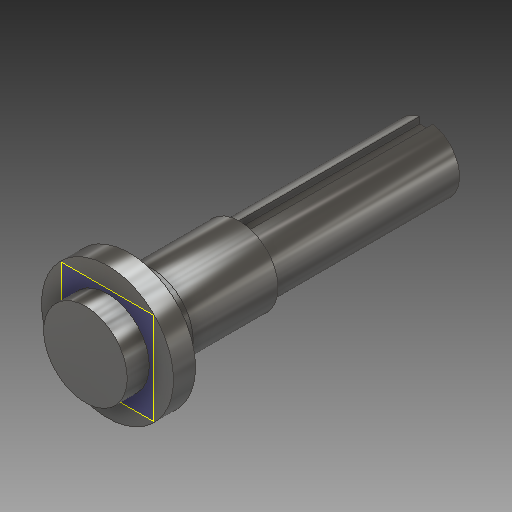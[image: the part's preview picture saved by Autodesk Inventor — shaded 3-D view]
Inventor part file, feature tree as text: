
AUTODESK INVENTOR PART (.ipt)
format: ipt  version: 2019 (Build 230136000, 136)  size: 156,672 bytes
history: native  units: in
note: dims shown in document units (in); Inventor stores cm internally (conversion verified against a paired STEP export)
features: sketch x5, other x3, plane x1
ambient origin geometry x8: Origin, YZ Plane, XZ Plane, XY Plane, X Axis, Y Axis, Z Axis, Center Point
bodies: Solid1 (feature_tree)
feature tree (9):
  other  "project handle part(1).ipt"
  other  "Solid1::project handle part(1).ipt"
  other  "TaggingFeature1"
  sketch  "Sketch1"  dims[d0=0.3937in]
  sketch  "Sketch2"
  sketch  "Sketch3"
  sketch  "Sketch4"
  sketch  "Sketch5"
  plane  "Work Plane1"
